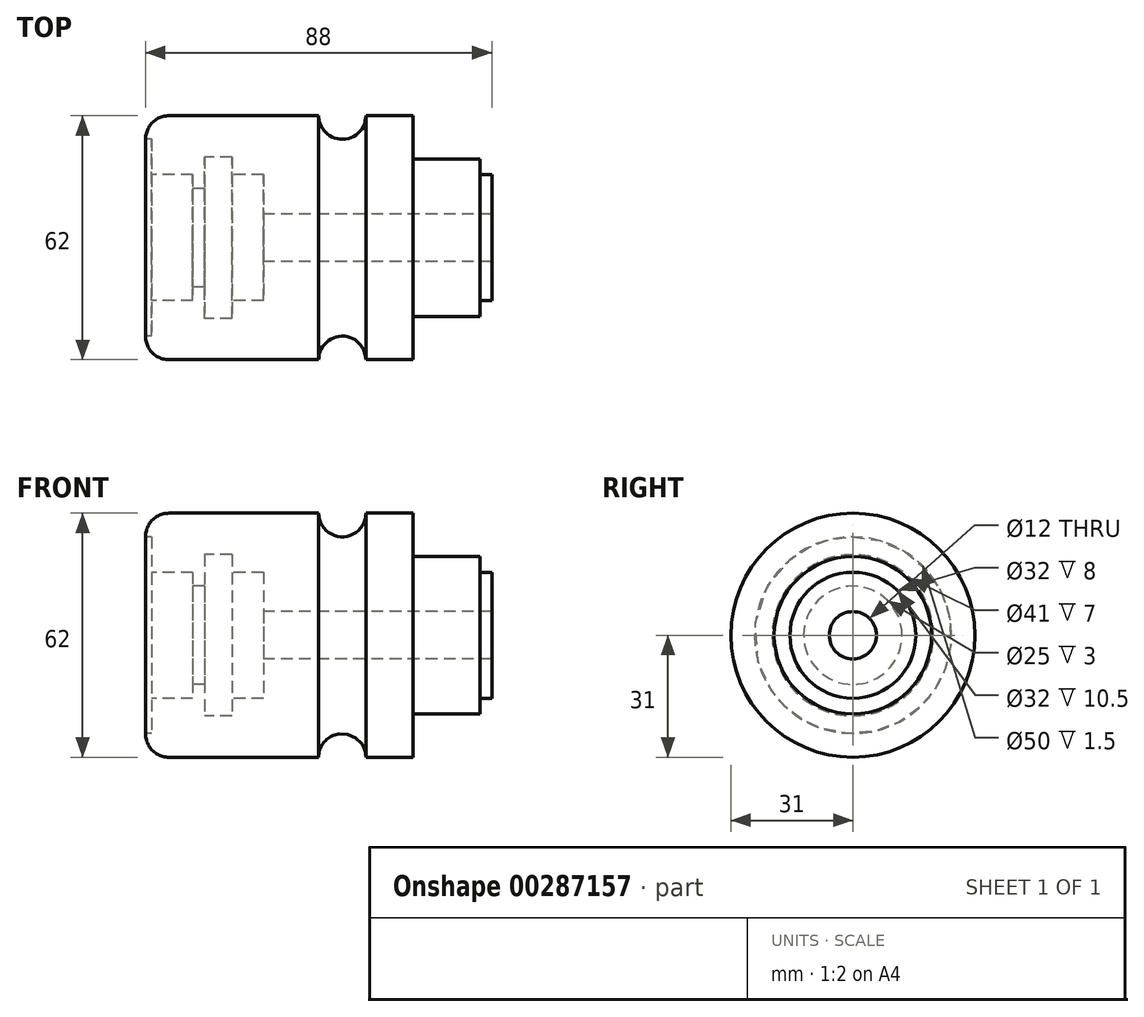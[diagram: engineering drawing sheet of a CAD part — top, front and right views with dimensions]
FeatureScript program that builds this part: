
annotation { "Feature Type Name" : "Feature", "Feature Type Description" : "" }
export const myFeature = defineFeature(function(context is Context, id is Id, definition is map)
    precondition{}
    {
        {
            var Q0;
            Q0=qCreatedBy(makeId("Front.planeOp"),FACE);
            var sketch = newSketch(context, id + "F0", { "sketchPlane" : qUnion([Q0])});
            skLineSegment(sketch, "E0", {"start": v(0, 0) * mm, "end": v(86.21, 0) * mm, "construction": true});
            skLineSegment(sketch, "E1", {"start": v(0, 0) * mm, "end": v(0, 31) * mm});
            skLineSegment(sketch, "E2", {"start": v(0, 31) * mm, "end": v(44, 31) * mm});
            skLineSegment(sketch, "E3", {"start": v(68, 31) * mm, "end": v(68, 20) * mm});
            skLineSegment(sketch, "E4", {"start": v(68, 20) * mm, "end": v(85, 20) * mm});
            skLineSegment(sketch, "E5", {"start": v(85, 20) * mm, "end": v(85, 16) * mm});
            skLineSegment(sketch, "E6", {"start": v(85, 16) * mm, "end": v(88, 16) * mm});
            skLineSegment(sketch, "E7", {"start": v(88, 16) * mm, "end": v(88, 0) * mm});
            skLineSegment(sketch, "E8", {"start": v(0, 0) * mm, "end": v(88, 0) * mm});
            skArc(sketch, "E9", {"start": v(44, 31) * mm, "mid": v(50, 25) * mm, "end": v(56, 31) * mm});
            skLineSegment(sketch, "E10.trimOffspring", {"start": v(56, 31) * mm, "end": v(68, 31) * mm});
            skSolve(sketch);
        }
        {
            var Q0;
            Q0=makeQuery(id+"F0.imprint","IMPRINT",FACE,{"disambiguationData":[TD([[makeQuery(id+"F0.imprint","IMPRINT",EDGE,{"derivedFrom":sQuery(id+"F0.wireOp",EDGE,"E1")}),-1.0]])]});
            var Q1;
            Q1=sQuery(id+"F0.wireOp",EDGE,"E8");
            revolve(context, id + "F1", {"entities" : qUnion([Q0]), "axis" : qUnion([Q1]), "revolveType" : RevolveType.FULL});
        }
        {
            var Q0;
            Q0=qCreatedBy(makeId("Front.planeOp"),FACE);
            var sketch = newSketch(context, id + "F2", { "sketchPlane" : qUnion([Q0])});
            skLineSegment(sketch, "E11", {"start": v(0, 0) * mm, "end": v(0, 25) * mm});
            skLineSegment(sketch, "E12", {"start": v(0, 25) * mm, "end": v(1.5, 25) * mm});
            skLineSegment(sketch, "E13", {"start": v(1.5, 25) * mm, "end": v(1.5, 16) * mm});
            skLineSegment(sketch, "E14", {"start": v(1.5, 16) * mm, "end": v(12, 16) * mm});
            skLineSegment(sketch, "E15", {"start": v(12, 16) * mm, "end": v(12, 12.5) * mm});
            skLineSegment(sketch, "E16", {"start": v(12, 12.5) * mm, "end": v(15, 12.5) * mm});
            skLineSegment(sketch, "E17", {"start": v(15, 12.5) * mm, "end": v(15, 20.5) * mm});
            skLineSegment(sketch, "E18", {"start": v(15, 20.5) * mm, "end": v(22, 20.5) * mm});
            skLineSegment(sketch, "E19", {"start": v(22, 20.5) * mm, "end": v(22, 16) * mm});
            skLineSegment(sketch, "E20", {"start": v(22, 16) * mm, "end": v(30, 16) * mm});
            skLineSegment(sketch, "E21", {"start": v(30, 16) * mm, "end": v(30, 6) * mm});
            skLineSegment(sketch, "E22", {"start": v(30, 6) * mm, "end": v(88, 6) * mm});
            skLineSegment(sketch, "E23", {"start": v(88, 6) * mm, "end": v(88, 0) * mm});
            skLineSegment(sketch, "E24", {"start": v(88, 0) * mm, "end": v(0, 0) * mm});
            skLineSegment(sketch, "E25", {"start": v(0, 0) * mm, "end": v(-46.5, 0) * mm, "construction": true});
            skSolve(sketch);
        }
        {
            var Q0;
            Q0 = qSketchRegion(id + "F2", true);
            var Q1;
            Q1=sQuery(id+"F2.wireOp",EDGE,"E24");
            revolve(context, id + "F3", {"operationType" : NewBodyOperationType.REMOVE, "entities" : qUnion([Q0]), "axis" : qUnion([Q1]), "revolveType" : RevolveType.FULL, "oppositeDirection" : true});
        }
        {
            var Q0;
            Q0=makeQuery(id+"F1.opRevolve","SWEPT_EDGE",EDGE,{"disambiguationData":[OSD([sQuery(id+"F0.wireOp",EDGE,"E1"),sQuery(id+"F0.wireOp",EDGE,"E2")])]});
            fillet(context, id + "F4", {"entities" : qUnion([Q0]), "radius" : 6 * mm, "tangentPropagation" : true, "allowEdgeOverflow" : false});
        }
    });
